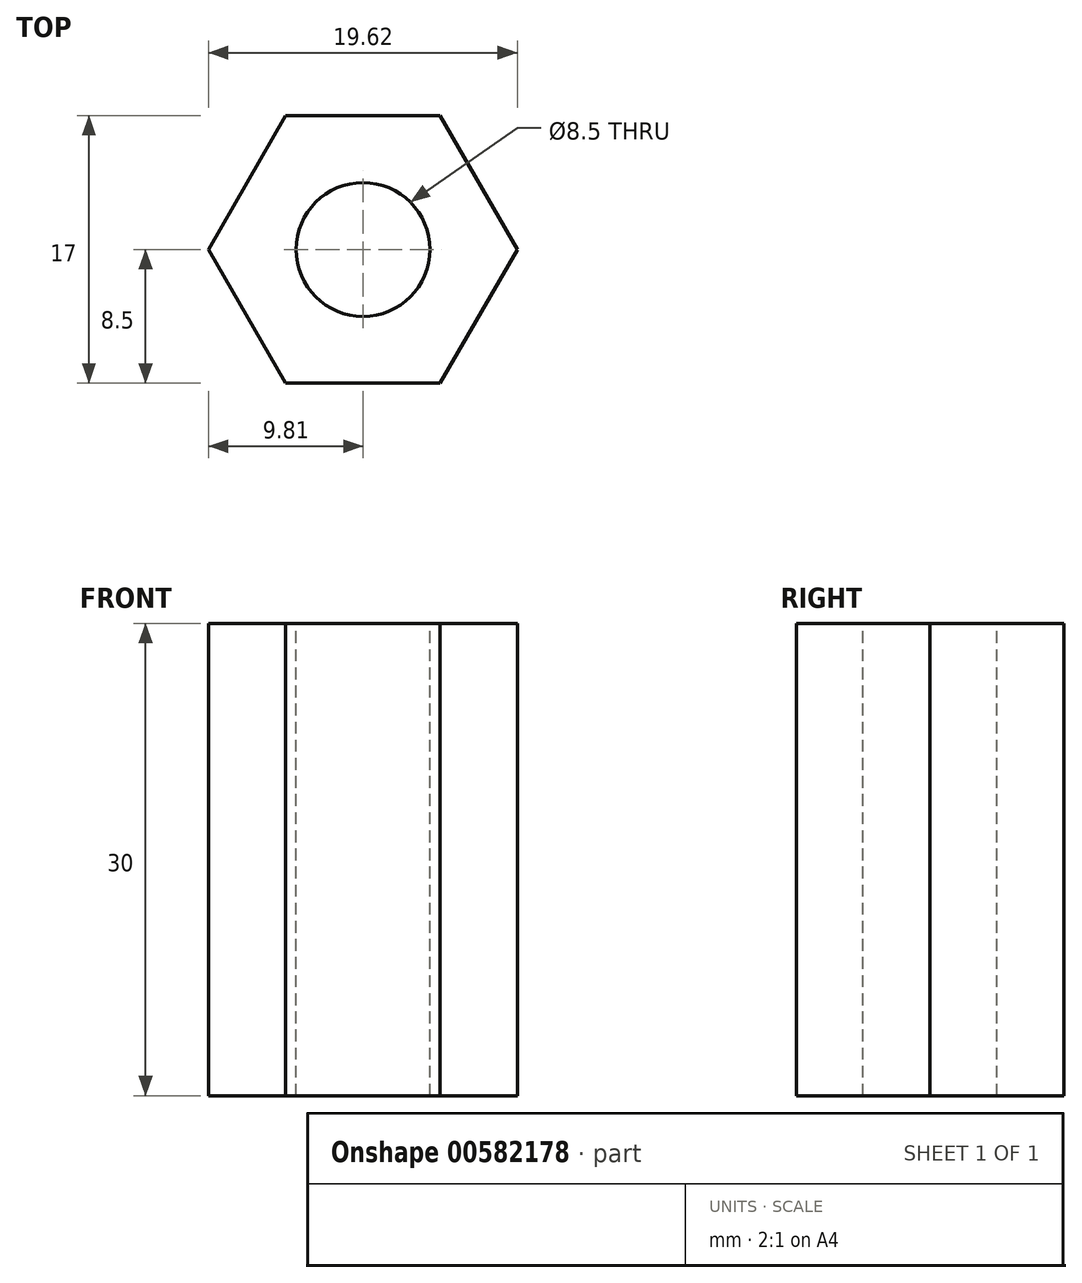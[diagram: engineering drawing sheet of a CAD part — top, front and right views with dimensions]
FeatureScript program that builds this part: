
annotation { "Feature Type Name" : "Feature", "Feature Type Description" : "" }
export const myFeature = defineFeature(function(context is Context, id is Id, definition is map)
    precondition{}
    {
        {
            var Q0;
            Q0=qCreatedBy(makeId("Top.planeOp"),FACE);
            var sketch = newSketch(context, id + "F0", { "sketchPlane" : qUnion([Q0])});
            skCircle(sketch, "E0.cCircle", {"center": v(0, 0) * mm, "radius": 8.5 * mm, "construction": true});
            skLineSegment(sketch, "E0.0", {"start": v(-4.9, 8.5) * mm, "end": v(4.9, 8.5) * mm});
            skLineSegment(sketch, "E0.1", {"start": v(4.9, 8.5) * mm, "end": v(9.81, 0) * mm});
            skLineSegment(sketch, "E0.2", {"start": v(9.81, 0) * mm, "end": v(4.9, -8.5) * mm});
            skLineSegment(sketch, "E0.3", {"start": v(4.9, -8.5) * mm, "end": v(-4.9, -8.5) * mm});
            skLineSegment(sketch, "E0.4", {"start": v(-4.9, -8.5) * mm, "end": v(-9.81, 0) * mm});
            skLineSegment(sketch, "E0.5", {"start": v(-9.81, 0) * mm, "end": v(-4.9, 8.5) * mm});
            skPoint(sketch, "E0.0.midPoint", {"position": v(0, 8.5) * mm});
            skSolve(sketch);
        }
        {
            var Q0;
            Q0=qSketchRegion(id+"F0",true);
            extrude(context, id + "F1", {"entities" : qUnion([Q0]), "depth" : 30 * mm, "offsetDistance" : 25 * mm});
        }
        {
            var Q0;
            Q0=makeQuery(id+"F1.opExtrude","CAP_FACE",FACE,{"disambiguationData":[OSD([sQuery(id+"F0.wireOp",EDGE,"E0.0"),sQuery(id+"F0.wireOp",EDGE,"E0.1"),sQuery(id+"F0.wireOp",EDGE,"E0.2"),sQuery(id+"F0.wireOp",EDGE,"E0.3"),sQuery(id+"F0.wireOp",EDGE,"E0.4"),sQuery(id+"F0.wireOp",EDGE,"E0.5")])],"isStart":false});
            var sketch = newSketch(context, id + "F2", { "sketchPlane" : qUnion([Q0])});
            skPoint(sketch, "E1", {"position": v(0, 0) * mm});
            skSolve(sketch);
        }
        {
            var Q0;
            Q0=sQuery(id+"F2.wireOp",VERTEX,"E1");
            var Q1;
            Q1=makeQuery(id+"F1.opExtrude","SWEPT_BODY",BODY,{"disambiguationData":[OSD([sQuery(id+"F0.wireOp",EDGE,"E0.0"),sQuery(id+"F0.wireOp",EDGE,"E0.1"),sQuery(id+"F0.wireOp",EDGE,"E0.2"),sQuery(id+"F0.wireOp",EDGE,"E0.3"),sQuery(id+"F0.wireOp",EDGE,"E0.4"),sQuery(id+"F0.wireOp",EDGE,"E0.5")])]});
            hole(context, id + "F3", {"style" : HoleStyle.SIMPLE, "endStyle" : HoleEndStyle.THROUGH, "standardTappedOrClearance" : lookupTablePath({ "standard" : "ISO", "engagement" : "75%", "pitch" : "1.5 mm", "size" : "M10", "type" : "Tapped" }), "standardBlindInLast" : lookupTablePath({ "standard" : "ISO", "engagement" : "75%", "pitch" : "1.5 mm", "size" : "M10", "type" : "Tapped" }), "holeDiameter" : 8.5 * mm, "showTappedDepth" : true, "isTappedThrough" : true, "tappedDepth" : 15.5 * mm, "tapClearance" : 3, "startFromSketch" : true, "locations" : qUnion([Q0]), "scope" : qUnion([Q1]), "majorDiameter" : 10 * mm});
        }
    });
